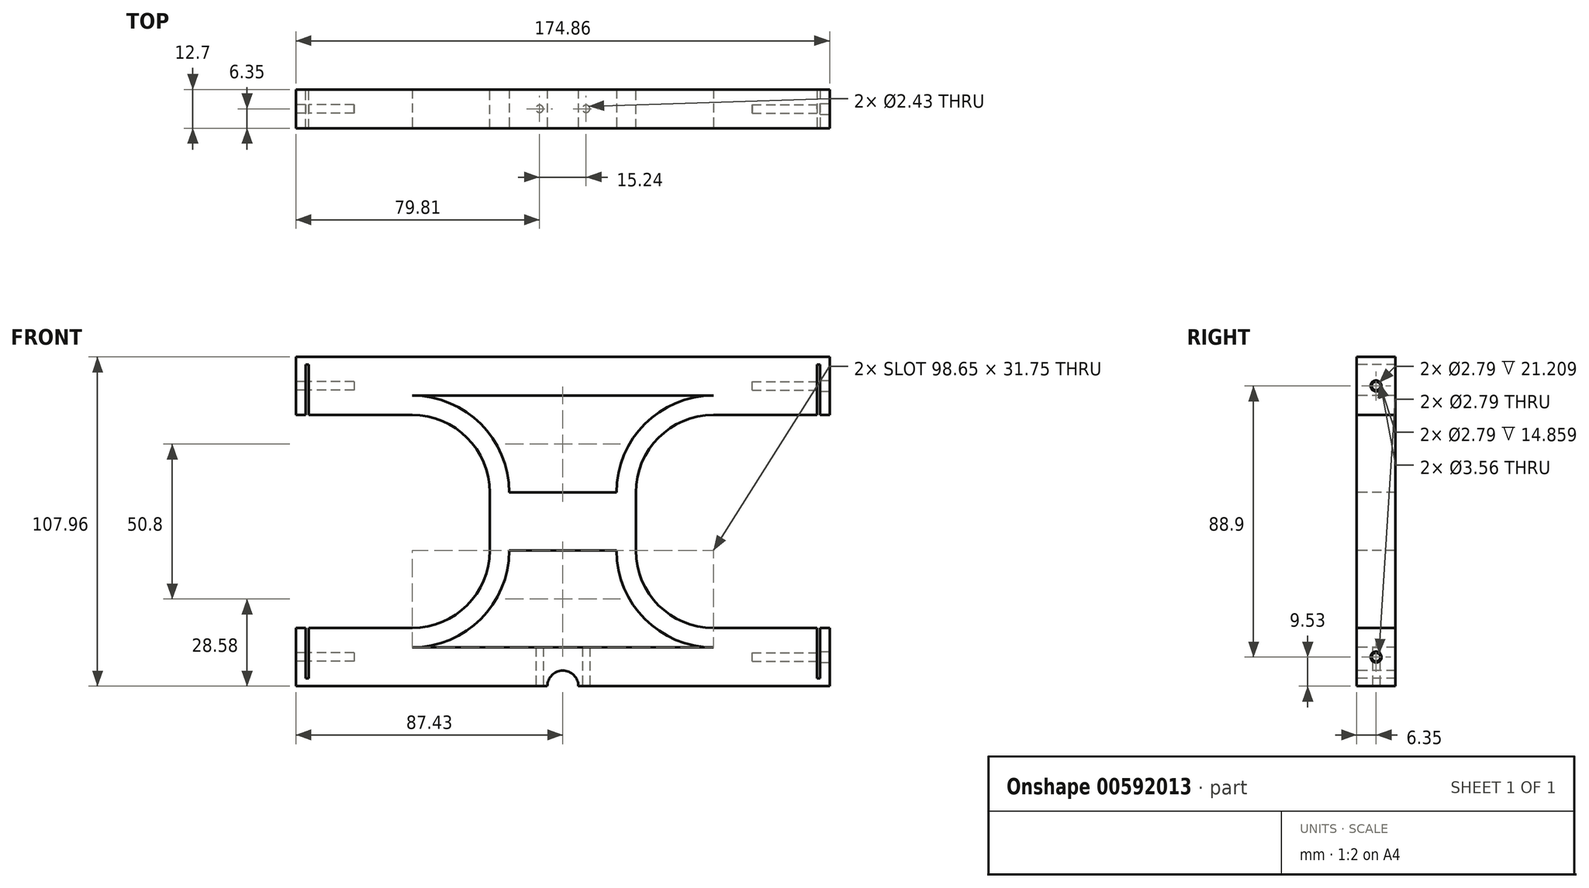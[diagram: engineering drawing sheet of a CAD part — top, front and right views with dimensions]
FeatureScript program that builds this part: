
annotation { "Feature Type Name" : "Feature", "Feature Type Description" : "" }
export const myFeature = defineFeature(function(context is Context, id is Id, definition is map)
    precondition{}
    {
        {
            var Q0;
            Q0=qCreatedBy(makeId("Front.planeOp"),FACE);
            var sketch = newSketch(context, id + "F0", { "sketchPlane" : qUnion([Q0])});
            skLineSegment(sketch, "E0.bottom", {"start": v(87.43, 53.98) * mm, "end": v(-87.43, 53.98) * mm});
            skLineSegment(sketch, "E0.top", {"start": v(87.43, -53.98) * mm, "end": v(-87.43, -53.98) * mm});
            skLineSegment(sketch, "E0.left", {"start": v(87.43, 53.97) * mm, "end": v(87.43, 34.93) * mm});
            skLineSegment(sketch, "E0.right", {"start": v(-87.43, 53.97) * mm, "end": v(-87.43, 34.92) * mm});
            skPoint(sketch, "E0.middle", {"position": v(0, 0) * mm});
            skLineSegment(sketch, "E1.bottom", {"start": v(-49.33, 34.92) * mm, "end": v(-87.43, 34.92) * mm});
            skLineSegment(sketch, "E1.top", {"start": v(-49.33, -34.93) * mm, "end": v(-87.43, -34.93) * mm});
            skLineSegment(sketch, "E1.left", {"start": v(-23.93, 9.52) * mm, "end": v(-23.93, -9.53) * mm});
            skPoint(sketch, "E1.middle", {"position": v(-87.43, 0) * mm});
            skPoint(sketch, "E1.right.start.orphan", {"position": v(-150.93, 34.92) * mm});
            skPoint(sketch, "E2.orphan", {"position": v(-150.93, -34.93) * mm});
            skLineSegment(sketch, "E3.trimOffspring", {"start": v(-87.43, 0) * mm, "end": v(-87.43, -53.97) * mm});
            skLineSegment(sketch, "E4", {"start": v(0, 53.97) * mm, "end": v(0, 22.48) * mm});
            skLineSegment(sketch, "E5.MirrorCS", {"start": v(49.33, 34.92) * mm, "end": v(87.43, 34.92) * mm});
            skLineSegment(sketch, "E6.MirrorCS", {"start": v(23.93, 9.52) * mm, "end": v(23.93, -9.53) * mm});
            skLineSegment(sketch, "E7.MirrorCS", {"start": v(49.33, -34.93) * mm, "end": v(87.43, -34.93) * mm});
            skLineSegment(sketch, "E8.trimOffspring", {"start": v(87.43, -34.92) * mm, "end": v(87.43, -53.97) * mm});
            skPoint(sketch, "E9.visualSharp", {"position": v(-23.93, 34.92) * mm});
            skArc(sketch, "E9.filletArc", {"start": v(-23.93, 9.52) * mm, "mid": v(-31.37, 27.49) * mm, "end": v(-49.33, 34.92) * mm});
            skPoint(sketch, "E10.visualSharp", {"position": v(-23.93, -34.93) * mm});
            skArc(sketch, "E10.filletArc", {"start": v(-49.33, -34.93) * mm, "mid": v(-31.37, -27.49) * mm, "end": v(-23.93, -9.53) * mm});
            skPoint(sketch, "E11.visualSharp", {"position": v(23.93, 34.93) * mm});
            skArc(sketch, "E11.filletArc", {"start": v(49.33, 34.92) * mm, "mid": v(31.37, 27.49) * mm, "end": v(23.93, 9.52) * mm});
            skPoint(sketch, "E12.visualSharp", {"position": v(23.93, -34.93) * mm});
            skArc(sketch, "E12.filletArc", {"start": v(23.93, -9.53) * mm, "mid": v(31.37, -27.49) * mm, "end": v(49.33, -34.93) * mm});
            skSolve(sketch);
        }
        {
            var Q0;
            Q0 = qSketchRegion(id + "F0", true);
            extrude(context, id + "F1", {"entities" : qUnion([Q0]), "depth" : 12.7 * mm, "offsetDistance" : 25.4 * mm});
        }
        {
            var Q0;
            Q0=makeQuery(id+"F1.opExtrude","CAP_FACE",FACE,{"disambiguationData":[OSD([sQuery(id+"F0.wireOp",EDGE,"E0.bottom"),sQuery(id+"F0.wireOp",EDGE,"E0.top"),sQuery(id+"F0.wireOp",EDGE,"E0.right"),sQuery(id+"F0.wireOp",EDGE,"E1.bottom"),sQuery(id+"F0.wireOp",EDGE,"E1.top"),sQuery(id+"F0.wireOp",EDGE,"E1.left"),sQuery(id+"F0.wireOp",EDGE,"E3.trimOffspring"),sQuery(id+"F0.wireOp",EDGE,"E0.left"),sQuery(id+"F0.wireOp",EDGE,"E5.MirrorCS"),sQuery(id+"F0.wireOp",EDGE,"E6.MirrorCS"),sQuery(id+"F0.wireOp",EDGE,"E7.MirrorCS"),sQuery(id+"F0.wireOp",EDGE,"E8.trimOffspring"),sQuery(id+"F0.wireOp",EDGE,"E9.filletArc"),sQuery(id+"F0.wireOp",EDGE,"E10.filletArc"),sQuery(id+"F0.wireOp",EDGE,"E11.filletArc"),sQuery(id+"F0.wireOp",EDGE,"E12.filletArc")])],"isStart":false});
            var sketch = newSketch(context, id + "F2", { "sketchPlane" : qUnion([Q0])});
            skLineSegment(sketch, "E13.bottom", {"start": v(-84.25, 51.43) * mm, "end": v(-83.24, 51.43) * mm});
            skLineSegment(sketch, "E13.top", {"start": v(-84.25, -51.44) * mm, "end": v(-83.24, -51.44) * mm});
            skLineSegment(sketch, "E13.left", {"start": v(-84.25, 51.43) * mm, "end": v(-84.25, -51.44) * mm});
            skLineSegment(sketch, "E13.right", {"start": v(-83.24, 51.43) * mm, "end": v(-83.24, -51.44) * mm});
            skPoint(sketch, "E13.middle", {"position": v(-83.74, 0) * mm});
            skLineSegment(sketch, "E14", {"start": v(0, 0) * mm, "end": v(0, 19.08) * mm});
            skLineSegment(sketch, "E15.MirrorCS", {"start": v(84.25, 51.43) * mm, "end": v(83.24, 51.43) * mm});
            skLineSegment(sketch, "E16.MirrorCS", {"start": v(84.25, -51.44) * mm, "end": v(83.24, -51.44) * mm});
            skLineSegment(sketch, "E17.MirrorCS", {"start": v(83.24, 51.43) * mm, "end": v(83.24, -51.44) * mm});
            skPoint(sketch, "E18.MirrorP", {"position": v(83.74, 0) * mm});
            skLineSegment(sketch, "E19.MirrorCS", {"start": v(84.25, 51.43) * mm, "end": v(84.25, -51.44) * mm});
            skSolve(sketch);
        }
        {
            var Q0;
            Q0 = qSketchRegion(id + "F2", true);
            extrude(context, id + "F3", {"entities" : qUnion([Q0]), "operationType" : NewBodyOperationType.REMOVE, "oppositeDirection" : true, "depth" : 25.4 * mm, "offsetDistance" : 25.4 * mm});
        }
        {
            var Q0;
            Q0=makeQuery(id+"F1.opExtrude","CAP_FACE",FACE,{"disambiguationData":[OSD([sQuery(id+"F0.wireOp",EDGE,"E0.bottom"),sQuery(id+"F0.wireOp",EDGE,"E0.top"),sQuery(id+"F0.wireOp",EDGE,"E0.right"),sQuery(id+"F0.wireOp",EDGE,"E1.bottom"),sQuery(id+"F0.wireOp",EDGE,"E1.top"),sQuery(id+"F0.wireOp",EDGE,"E1.left"),sQuery(id+"F0.wireOp",EDGE,"E3.trimOffspring"),sQuery(id+"F0.wireOp",EDGE,"E0.left"),sQuery(id+"F0.wireOp",EDGE,"E5.MirrorCS"),sQuery(id+"F0.wireOp",EDGE,"E6.MirrorCS"),sQuery(id+"F0.wireOp",EDGE,"E7.MirrorCS"),sQuery(id+"F0.wireOp",EDGE,"E8.trimOffspring"),sQuery(id+"F0.wireOp",EDGE,"E9.filletArc"),sQuery(id+"F0.wireOp",EDGE,"E10.filletArc"),sQuery(id+"F0.wireOp",EDGE,"E11.filletArc"),sQuery(id+"F0.wireOp",EDGE,"E12.filletArc")])],"isStart":false});
            var sketch = newSketch(context, id + "F4", { "sketchPlane" : qUnion([Q0])});
            skCircle(sketch, "E20", {"center": v(0, -53.98) * mm, "radius": 5.08 * mm});
            skSolve(sketch);
        }
        {
            var Q0;
            Q0 = qSketchRegion(id + "F4", true);
            extrude(context, id + "F5", {"entities" : qUnion([Q0]), "operationType" : NewBodyOperationType.REMOVE, "oppositeDirection" : true, "depth" : 25.4 * mm, "offsetDistance" : 25.4 * mm});
        }
        {
            var Q0;
            {var subQ9=sQuery(id+"F0.wireOp",EDGE,"E3.trimOffspring");var subQ14=sQuery(id+"F0.wireOp",EDGE,"E0.top");Q0=makeQuery(id+"F5.boolean.opBoolean","SPLIT",FACE,{"disambiguationData":[TD([makeQuery(id+"F1.opExtrude","SWEPT_FACE",FACE,{"disambiguationData":[OSD([subQ9])]})])],"derivedFrom":makeQuery(id+"F1.opExtrude","SWEPT_FACE",FACE,{"disambiguationData":[OSD([subQ14])]})});}
            var sketch = newSketch(context, id + "F6", { "sketchPlane" : qUnion([Q0])});
            skCircle(sketch, "E21", {"center": v(-7.62, 6.35) * mm, "radius": 1.22 * mm});
            skPoint(sketch, "E21.centerSnap0", {"position": v(-87.43, 6.35) * mm});
            skLineSegment(sketch, "E22", {"start": v(0, 0) * mm, "end": v(0, -12.7) * mm});
            skCircle(sketch, "E23.MirrorC", {"center": v(7.62, 6.35) * mm, "radius": 1.22 * mm});
            skSolve(sketch);
        }
        {
            var Q0;
            Q0 = qSketchRegion(id + "F6", true);
            extrude(context, id + "F7", {"entities" : qUnion([Q0]), "operationType" : NewBodyOperationType.REMOVE, "oppositeDirection" : true, "depth" : 25.4 * mm, "offsetDistance" : 25.4 * mm});
        }
        {
            var Q0;
            Q0=makeQuery(id+"F1.opExtrude","SWEPT_FACE",FACE,{"disambiguationData":[OSD([sQuery(id+"F0.wireOp",EDGE,"E0.left")])]});
            var sketch = newSketch(context, id + "F8", { "sketchPlane" : qUnion([Q0])});
            skCircle(sketch, "E24", {"center": v(-6.35, 44.45) * mm, "radius": 1.4 * mm});
            skPoint(sketch, "E24.centerSnap0", {"position": v(-6.35, 53.98) * mm});
            skLineSegment(sketch, "E25", {"start": v(0, 0) * mm, "end": v(31.37, 0) * mm});
            skCircle(sketch, "E26.MirrorC", {"center": v(-6.35, -44.45) * mm, "radius": 1.4 * mm});
            skSolve(sketch);
        }
        {
            var Q0;
            Q0 = qSketchRegion(id + "F8", true);
            extrude(context, id + "F9", {"entities" : qUnion([Q0]), "operationType" : NewBodyOperationType.REMOVE, "oppositeDirection" : true, "depth" : 25.4 * mm, "offsetDistance" : 25.4 * mm});
        }
        {
            var Q0;
            Q0=makeQuery(id+"F1.opExtrude","SWEPT_FACE",FACE,{"disambiguationData":[OSD([sQuery(id+"F0.wireOp",EDGE,"E0.right")])]});
            var sketch = newSketch(context, id + "F10", { "sketchPlane" : qUnion([Q0])});
            skCircle(sketch, "E27.0", {"center": v(6.35, 44.45) * mm, "radius": 1.4 * mm});
            skCircle(sketch, "E28.0", {"center": v(6.35, -44.45) * mm, "radius": 1.4 * mm});
            skSolve(sketch);
        }
        {
            var Q0;
            Q0 = qSketchRegion(id + "F10", true);
            extrude(context, id + "F11", {"entities" : qUnion([Q0]), "operationType" : NewBodyOperationType.REMOVE, "oppositeDirection" : true, "depth" : 19.05 * mm, "offsetDistance" : 25.4 * mm});
        }
        {
            var Q0;
            Q0=makeQuery(id+"F1.opExtrude","SWEPT_FACE",FACE,{"disambiguationData":[OSD([sQuery(id+"F0.wireOp",EDGE,"E0.left")])]});
            var sketch = newSketch(context, id + "F12", { "sketchPlane" : qUnion([Q0])});
            skCircle(sketch, "E29", {"center": v(-6.35, 44.45) * mm, "radius": 1.78 * mm});
            skLineSegment(sketch, "E30", {"start": v(0, 0) * mm, "end": v(26.27, 0) * mm});
            skCircle(sketch, "E31.MirrorC", {"center": v(-6.35, -44.45) * mm, "radius": 1.78 * mm});
            skSolve(sketch);
        }
        {
            var Q0;
            Q0 = qSketchRegion(id + "F12", true);
            extrude(context, id + "F13", {"entities" : qUnion([Q0]), "operationType" : NewBodyOperationType.REMOVE, "oppositeDirection" : true, "depth" : 3.17 * mm, "offsetDistance" : 25.4 * mm});
        }
        {
            var Q0;
            Q0=makeQuery(id+"F1.opExtrude","CAP_FACE",FACE,{"disambiguationData":[OSD([sQuery(id+"F0.wireOp",EDGE,"E0.bottom"),sQuery(id+"F0.wireOp",EDGE,"E0.top"),sQuery(id+"F0.wireOp",EDGE,"E0.right"),sQuery(id+"F0.wireOp",EDGE,"E1.bottom"),sQuery(id+"F0.wireOp",EDGE,"E1.top"),sQuery(id+"F0.wireOp",EDGE,"E1.left"),sQuery(id+"F0.wireOp",EDGE,"E3.trimOffspring"),sQuery(id+"F0.wireOp",EDGE,"E0.left"),sQuery(id+"F0.wireOp",EDGE,"E5.MirrorCS"),sQuery(id+"F0.wireOp",EDGE,"E6.MirrorCS"),sQuery(id+"F0.wireOp",EDGE,"E7.MirrorCS"),sQuery(id+"F0.wireOp",EDGE,"E8.trimOffspring"),sQuery(id+"F0.wireOp",EDGE,"E9.filletArc"),sQuery(id+"F0.wireOp",EDGE,"E10.filletArc"),sQuery(id+"F0.wireOp",EDGE,"E11.filletArc"),sQuery(id+"F0.wireOp",EDGE,"E12.filletArc")])],"isStart":false});
            var sketch = newSketch(context, id + "F14", { "sketchPlane" : qUnion([Q0])});
            skArc(sketch, "E32.0", {"start": v(-49.33, -41.28) * mm, "mid": v(-26.88, -31.98) * mm, "end": v(-17.58, -9.53) * mm});
            skLineSegment(sketch, "E32.1", {"start": v(-17.58, 9.52) * mm, "end": v(-17.58, -9.53) * mm});
            skArc(sketch, "E32.2", {"start": v(-17.58, 9.52) * mm, "mid": v(-26.88, 31.98) * mm, "end": v(-49.33, 41.27) * mm});
            skArc(sketch, "E33.0", {"start": v(17.58, -9.53) * mm, "mid": v(26.88, -31.98) * mm, "end": v(49.33, -41.28) * mm});
            skLineSegment(sketch, "E33.1", {"start": v(17.58, 9.52) * mm, "end": v(17.58, -9.53) * mm});
            skArc(sketch, "E33.2", {"start": v(49.33, 41.27) * mm, "mid": v(26.88, 31.98) * mm, "end": v(17.58, 9.52) * mm});
            skLineSegment(sketch, "E34", {"start": v(-49.33, 41.27) * mm, "end": v(49.33, 41.27) * mm});
            skLineSegment(sketch, "E35", {"start": v(-49.33, -41.28) * mm, "end": v(49.33, -41.28) * mm});
            skSolve(sketch);
        }
        {
            var Q0;
            Q0 = qSketchRegion(id + "F14", true);
            extrude(context, id + "F15", {"entities" : qUnion([Q0]), "operationType" : NewBodyOperationType.REMOVE, "oppositeDirection" : true, "depth" : 25.4 * mm, "offsetDistance" : 25.4 * mm});
        }
        {
            var Q0;
            Q0=makeQuery(id+"F15.boolean.opBoolean","COPY",FACE,{"derivedFrom":makeQuery(id+"F15.opExtrude","SWEPT_FACE",FACE,{"disambiguationData":[OSD([sQuery(id+"F14.wireOp",EDGE,"E32.1")])]})});
            var sketch = newSketch(context, id + "F16", { "sketchPlane" : qUnion([Q0])});
            skLineSegment(sketch, "E36.0.0", {"start": v(0, 9.52) * mm, "end": v(-12.7, 9.52) * mm});
            skLineSegment(sketch, "E36.0.1", {"start": v(-12.7, 9.52) * mm, "end": v(-12.7, -9.53) * mm});
            skLineSegment(sketch, "E36.0.2", {"start": v(-12.7, -9.53) * mm, "end": v(0, -9.53) * mm});
            skLineSegment(sketch, "E36.0.3", {"start": v(0, -9.53) * mm, "end": v(0, 9.52) * mm});
            skSolve(sketch);
        }
        {
            var Q0;
            Q0 = qSketchRegion(id + "F16", true);
            extrude(context, id + "F17", {"entities" : qUnion([Q0]), "operationType" : NewBodyOperationType.ADD, "depth" : 38.1 * mm, "offsetDistance" : 25.4 * mm});
        }
    });
